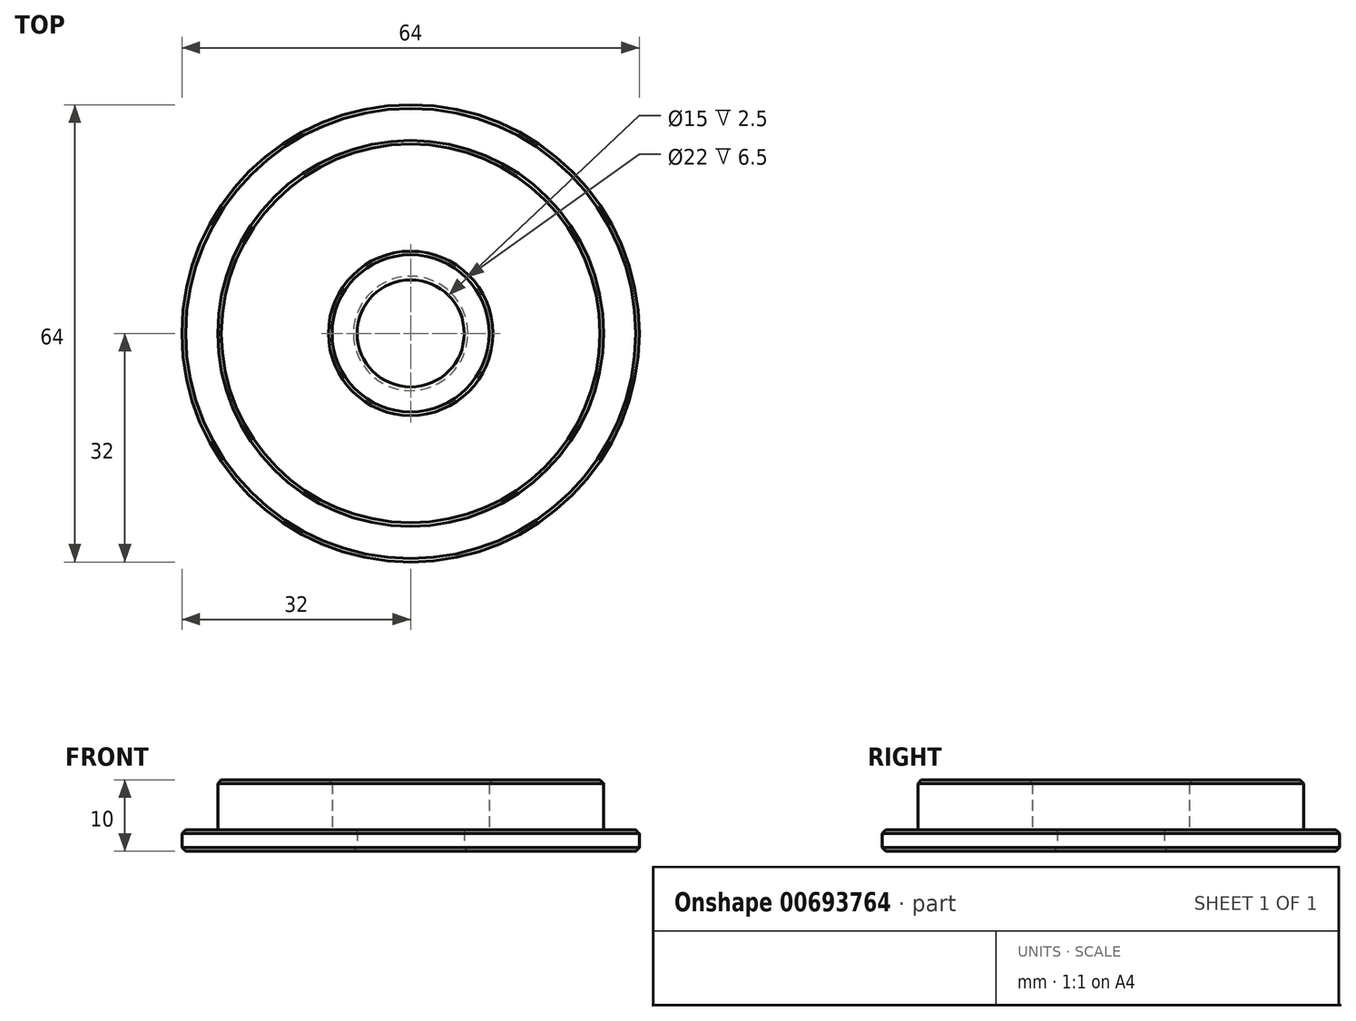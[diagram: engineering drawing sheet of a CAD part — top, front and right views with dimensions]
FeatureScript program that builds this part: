
annotation { "Feature Type Name" : "Feature", "Feature Type Description" : "" }
export const myFeature = defineFeature(function(context is Context, id is Id, definition is map)
    precondition{}
    {
        {
            var Q0;
            Q0=qCreatedBy(makeId("Top.planeOp"),FACE);
            var sketch = newSketch(context, id + "F0", { "sketchPlane" : qUnion([Q0])});
            skCircle(sketch, "E0", {"center": v(0, 0) * mm, "radius": 32 * mm});
            skCircle(sketch, "E1", {"center": v(0, 0) * mm, "radius": 7.5 * mm});
            skSolve(sketch);
        }
        {
            var Q0;
            Q0 = qSketchRegion(id + "F0", true);
            extrude(context, id + "F1", {"entities" : qUnion([Q0]), "depth" : 3 * mm, "offsetDistance" : 25 * mm});
        }
        {
            var Q0;
            Q0=makeQuery(id+"F1.opExtrude","CAP_FACE",FACE,{"disambiguationData":[OSD([sQuery(id+"F0.wireOp",EDGE,"E0"),sQuery(id+"F0.wireOp",EDGE,"E1")])],"isStart":false});
            var sketch = newSketch(context, id + "F2", { "sketchPlane" : qUnion([Q0])});
            skCircle(sketch, "E2", {"center": v(0, 0) * mm, "radius": 27 * mm});
            skCircle(sketch, "E3", {"center": v(0, 0) * mm, "radius": 11 * mm});
            skSolve(sketch);
        }
        {
            var Q0;
            Q0 = qSketchRegion(id + "F2", true);
            extrude(context, id + "F3", {"entities" : qUnion([Q0]), "operationType" : NewBodyOperationType.ADD, "depth" : 7 * mm, "offsetDistance" : 25 * mm});
        }
        {
            var Q0;
            Q0=makeQuery(id+"F3.opExtrude","CAP_EDGE",EDGE,{"disambiguationData":[OSD([sQuery(id+"F2.wireOp",EDGE,"E2")])],"isStart":false});
            var Q1;
            Q1=makeQuery(id+"F1.opExtrude","CAP_EDGE",EDGE,{"disambiguationData":[OSD([sQuery(id+"F0.wireOp",EDGE,"E0")])],"isStart":false});
            var Q2;
            Q2=makeQuery(id+"F3.opExtrude","CAP_EDGE",EDGE,{"disambiguationData":[OSD([sQuery(id+"F2.wireOp",EDGE,"E3")])],"isStart":false});
            var Q3;
            Q3=makeQuery(id+"F1.opExtrude","CAP_EDGE",EDGE,{"disambiguationData":[OSD([sQuery(id+"F0.wireOp",EDGE,"E0")])],"isStart":true});
            var Q4;
            Q4=makeQuery(id+"F1.opExtrude","CAP_EDGE",EDGE,{"disambiguationData":[OSD([sQuery(id+"F0.wireOp",EDGE,"E1")])],"isStart":true});
            chamfer(context, id + "F4", {"entities" : qUnion([Q0, Q1, Q2, Q3, Q4]), "width" : .5 * mm, "tangentPropagation" : true});
        }
    });
